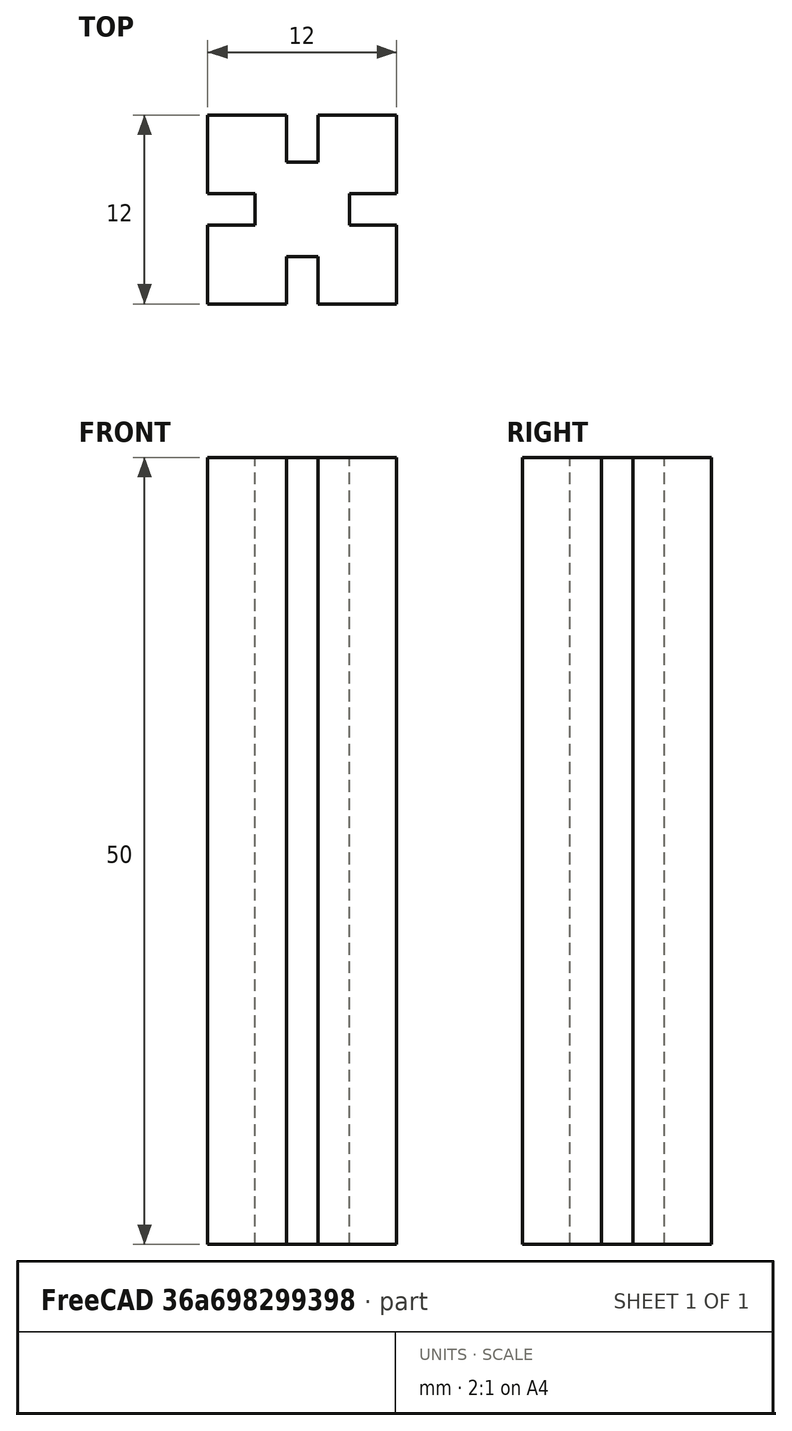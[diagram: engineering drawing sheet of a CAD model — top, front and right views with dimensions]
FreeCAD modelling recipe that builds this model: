
FCSTD DOCUMENT  (FreeCAD 0.19R)
Label: maze_pillar
License: All rights reserved
LicenseURL: http://en.wikipedia.org/wiki/All_rights_reserved
objects: Sketcher::SketchObject×1, PartDesign::Pad×1, PartDesign::Body×1
note: 4 computed .brp shape members not serialized (recipe doc carries the construction recipe); baked Part::Feature solids carry a one-line shape summary decoded from their .brp

FEATURE [Sketcher::SketchObject] Sketch
  FullyConstrained = true
  MapMode = 5
  Support = -> [XY_Plane]
  sketch-geometry (20):
    g0: LineSegment StartX=0 StartY=0 StartZ=0 EndX=5 EndY=0 EndZ=0
    g1: LineSegment StartX=12 StartY=0 StartZ=0 EndX=12 EndY=5 EndZ=0
    g2: LineSegment StartX=12 StartY=12 StartZ=0 EndX=7 EndY=12 EndZ=0
    g3: LineSegment StartX=0 StartY=12 StartZ=0 EndX=0 EndY=7 EndZ=0
    g4: LineSegment StartX=0 StartY=7 StartZ=0 EndX=3 EndY=7 EndZ=0
    g5: LineSegment StartX=3 StartY=7 StartZ=0 EndX=3 EndY=5 EndZ=0
    g6: LineSegment StartX=3 StartY=5 StartZ=0 EndX=0 EndY=5 EndZ=0
    g7: LineSegment StartX=5 StartY=0 StartZ=0 EndX=5 EndY=3 EndZ=0
    g8: LineSegment StartX=5 StartY=3 StartZ=0 EndX=7 EndY=3 EndZ=0
    g9: LineSegment StartX=7 StartY=3 StartZ=0 EndX=7 EndY=0 EndZ=0
    g10: LineSegment StartX=12 StartY=5 StartZ=0 EndX=9 EndY=5 EndZ=0
    g11: LineSegment StartX=9 StartY=5 StartZ=0 EndX=9 EndY=7 EndZ=0
    g12: LineSegment StartX=9 StartY=7 StartZ=0 EndX=12 EndY=7 EndZ=0
    g13: LineSegment StartX=5 StartY=12 StartZ=0 EndX=5 EndY=9 EndZ=0
    g14: LineSegment StartX=5 StartY=9 StartZ=0 EndX=7 EndY=9 EndZ=0
    g15: LineSegment StartX=7 StartY=9 StartZ=0 EndX=7 EndY=12 EndZ=0
    g16: LineSegment StartX=0 StartY=5 StartZ=0 EndX=0 EndY=0 EndZ=0
    g17: LineSegment StartX=5 StartY=12 StartZ=0 EndX=0 EndY=12 EndZ=0
    g18: LineSegment StartX=12 StartY=7 StartZ=0 EndX=12 EndY=12 EndZ=0
    g19: LineSegment StartX=7 StartY=0 StartZ=0 EndX=12 EndY=0 EndZ=0
  constraints (55):
    c: Coincident(g19,g1)
    c: Coincident(g18,g2)
    c: Coincident(g17,g3)
    c: Coincident(g16,g0)
    c: Horizontal(g0)
    c: Horizontal(g2)
    c: Vertical(g1)
    c: Vertical(g3)
    c: Coincident(g0,g-1)
    c: Horizontal(g4)
    c: Coincident(g4,g5)
    c: Vertical(g5)
    c: Coincident(g5,g6)
    c: Horizontal(g6)
    c: Vertical(g7)
    c: Coincident(g7,g8)
    c: Horizontal(g8)
    c: Coincident(g8,g9)
    c: Vertical(g9)
    c: Horizontal(g10)
    c: Coincident(g10,g11)
    c: Vertical(g11)
    c: Coincident(g11,g12)
    c: Horizontal(g12)
    c: Vertical(g13)
    c: Coincident(g13,g14)
    c: Horizontal(g14)
    c: Coincident(g14,g15)
    c: Vertical(g15)
    c: Distance(g4) = 3
    c: Distance(g13) = 3
    c: Distance(g12) = 3
    c: Distance(g9) = 3
    c: Distance(g5) = 2
    c: Distance(g14) = 2
    c: Distance(g11) = 2
    c: Distance(g17,g4) = 5
    c: Distance(g17,g13) = 5
    c: Distance(g19,g9) = 5
    c: Distance(g19,g10) = 5
    c: Distance(g8) = 2
    c: DistanceX(g-2,g19) = 12
    c: DistanceY(g-1,g17) = 12
    c: Coincident(g3,g4)
    c: Coincident(g16,g6)
    c: Tangent(g3,g16)
    c: Coincident(g2,g15)
    c: Coincident(g17,g13)
    c: Tangent(g2,g17)
    c: Coincident(g1,g10)
    c: Coincident(g18,g12)
    c: Tangent(g1,g18)
    c: Coincident(g0,g7)
    c: Coincident(g19,g9)
    c: Tangent(g0,g19)
FEATURE [PartDesign::Pad] Pad
  Direction = (1,1,1)
  Length = 50
  Length2 = 100
  Profile = -> Sketch
  Type = 0
FEATURE [PartDesign::Body] Body
  Group = -> [Sketch,Pad]
  Origin = -> Origin
  Tip = -> Pad
